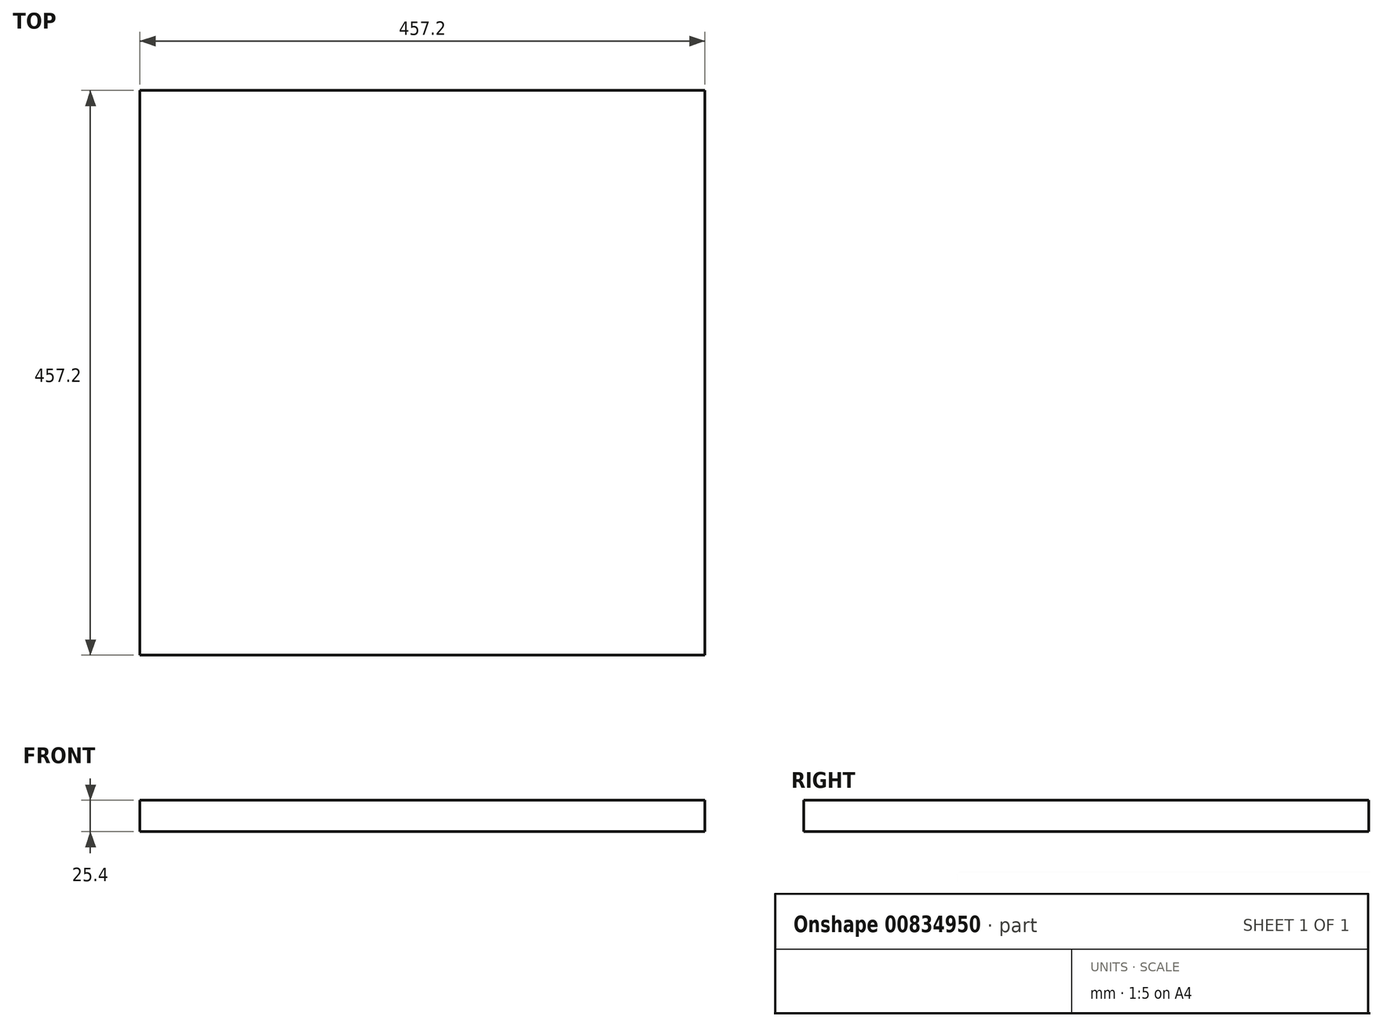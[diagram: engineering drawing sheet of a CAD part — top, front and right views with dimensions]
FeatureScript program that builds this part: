
annotation { "Feature Type Name" : "Feature", "Feature Type Description" : "" }
export const myFeature = defineFeature(function(context is Context, id is Id, definition is map)
    precondition{}
    {
        {
            var Q0;
            Q0=qCreatedBy(makeId("Top.planeOp"),FACE);
            var sketch = newSketch(context, id + "F0", { "sketchPlane" : qUnion([Q0])});
            skLineSegment(sketch, "E0.bottom", {"start": v(0, 0) * mm, "end": v(457.2, 0) * mm});
            skLineSegment(sketch, "E0.top", {"start": v(0, 457.2) * mm, "end": v(457.2, 457.2) * mm});
            skLineSegment(sketch, "E0.left", {"start": v(0, 0) * mm, "end": v(0, 457.2) * mm});
            skLineSegment(sketch, "E0.right", {"start": v(457.2, 0) * mm, "end": v(457.2, 457.2) * mm});
            skSolve(sketch);
        }
        {
            var Q0;
            Q0 = qSketchRegion(id + "F0", true);
            extrude(context, id + "F1", {"entities" : qUnion([Q0]), "depth" : 25.4 * mm, "offsetDistance" : 25.4 * mm});
        }
    });
